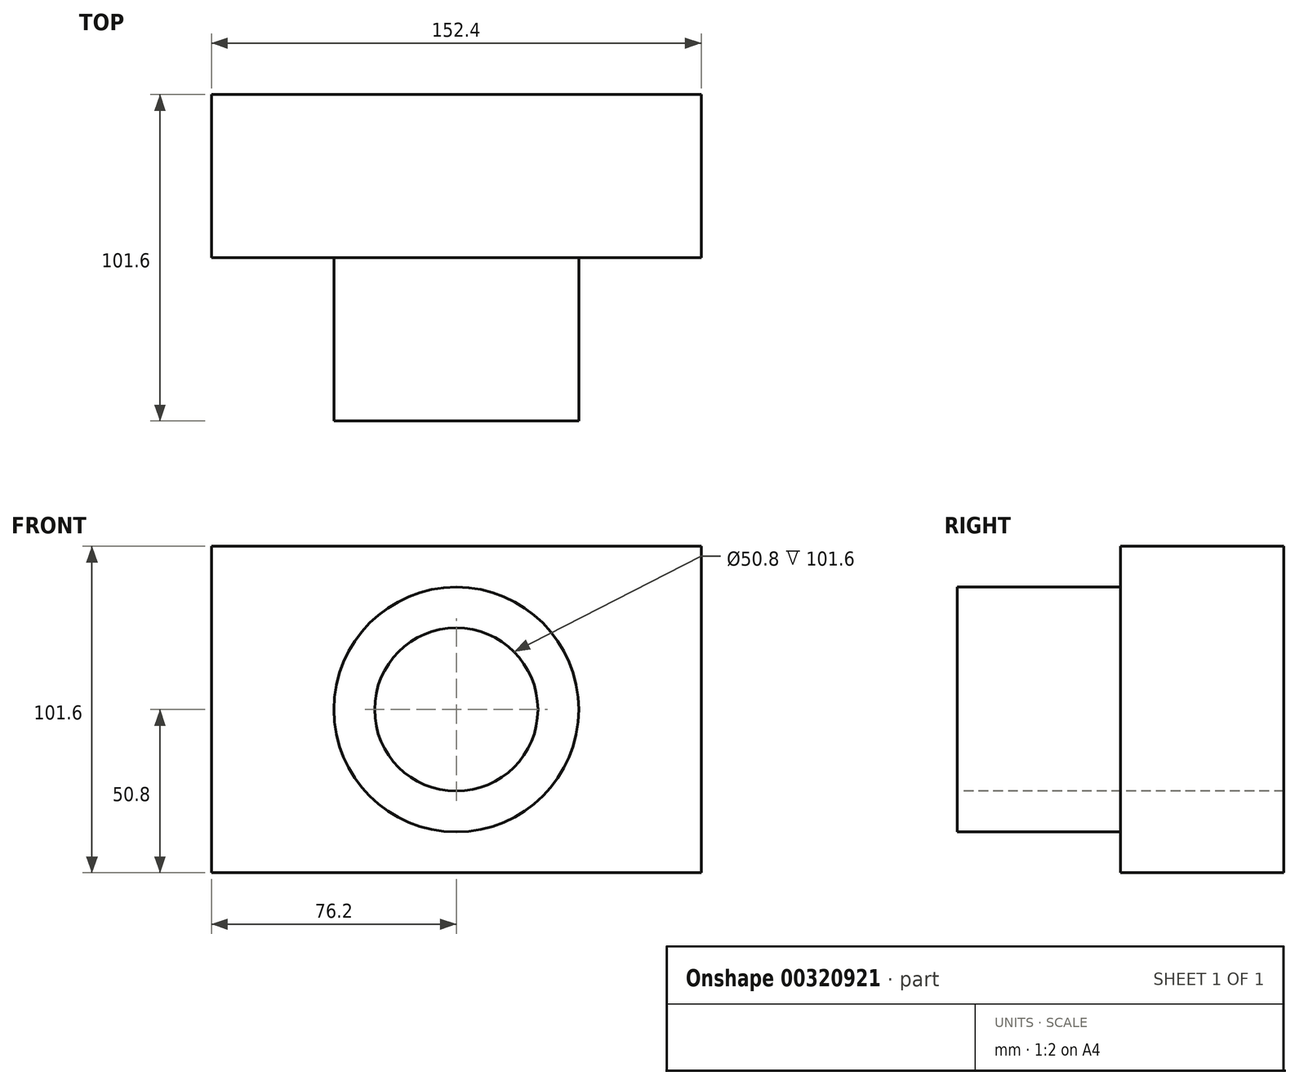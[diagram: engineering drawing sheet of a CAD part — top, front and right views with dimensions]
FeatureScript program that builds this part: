
annotation { "Feature Type Name" : "Feature", "Feature Type Description" : "" }
export const myFeature = defineFeature(function(context is Context, id is Id, definition is map)
    precondition{}
    {
        {
            var Q0;
            Q0=qCreatedBy(makeId("Front.planeOp"),FACE);
            var sketch = newSketch(context, id + "F0", { "sketchPlane" : qUnion([Q0])});
            skLineSegment(sketch, "E0.bottom", {"start": v(-76.2, 50.8) * mm, "end": v(76.2, 50.8) * mm});
            skLineSegment(sketch, "E0.top", {"start": v(-76.2, -50.8) * mm, "end": v(76.2, -50.8) * mm});
            skLineSegment(sketch, "E0.left", {"start": v(-76.2, 50.8) * mm, "end": v(-76.2, -50.8) * mm});
            skLineSegment(sketch, "E0.right", {"start": v(76.2, 50.8) * mm, "end": v(76.2, -50.8) * mm});
            skSolve(sketch);
        }
        {
            var Q0;
            Q0=makeQuery(id+"F0.imprint","IMPRINT",FACE,{"disambiguationData":[TD([[makeQuery(id+"F0.imprint","IMPRINT",EDGE,{"derivedFrom":sQuery(id+"F0.wireOp",EDGE,"E0.bottom")}),-1.0]])]});
            extrude(context, id + "F1", {"entities" : qUnion([Q0]), "depth" : 50.8 * mm});
        }
        {
            var Q0;
            Q0=makeQuery(id+"F1.opExtrude","CAP_FACE",FACE,{"disambiguationData":[OSD([sQuery(id+"F0.wireOp",EDGE,"E0.bottom"),sQuery(id+"F0.wireOp",EDGE,"E0.top"),sQuery(id+"F0.wireOp",EDGE,"E0.left"),sQuery(id+"F0.wireOp",EDGE,"E0.right")])],"isStart":false});
            var sketch = newSketch(context, id + "F2", { "sketchPlane" : qUnion([Q0])});
            skSolve(sketch);
        }
        {
            var Q0;
            Q0=makeQuery(id+"F2.imprint","IMPRINT",FACE,{"disambiguationData":[TD([[makeQuery(id+"F2.imprint","IMPRINT",EDGE,{"derivedFrom":makeQuery(id+"F1.opExtrude","CAP_EDGE",EDGE,{"disambiguationData":[OSD([sQuery(id+"F0.wireOp",EDGE,"E0.bottom")])],"isStart":false})}),-1.0]])]});
            var sketch = newSketch(context, id + "F3", { "sketchPlane" : qUnion([Q0])});
            skCircle(sketch, "E1", {"center": v(0, 0) * mm, "radius": 38.1 * mm});
            skSolve(sketch);
        }
        {
            var Q0;
            Q0=makeQuery(id+"F3.imprint","IMPRINT",FACE,{"disambiguationData":[TD([[makeQuery(id+"F3.imprint","IMPRINT",EDGE,{"derivedFrom":sQuery(id+"F3.wireOp",EDGE,"E1")}),1.0]])]});
            extrude(context, id + "F4", {"entities" : qUnion([Q0]), "operationType" : NewBodyOperationType.ADD, "depth" : 50.8 * mm});
        }
        {
            var Q0;
            Q0=makeQuery(id+"F4.opExtrude","CAP_FACE",FACE,{"disambiguationData":[OSD([sQuery(id+"F3.wireOp",EDGE,"E1")])],"isStart":false});
            var sketch = newSketch(context, id + "F5", { "sketchPlane" : qUnion([Q0])});
            skCircle(sketch, "E2", {"center": v(0, 0) * mm, "radius": 25.4 * mm});
            skSolve(sketch);
        }
        {
            var Q0;
            Q0=makeQuery(id+"F5.imprint","IMPRINT",FACE,{"disambiguationData":[TD([[makeQuery(id+"F5.imprint","IMPRINT",EDGE,{"derivedFrom":sQuery(id+"F5.wireOp",EDGE,"E2")}),1.0]])]});
            extrude(context, id + "F6", {"entities" : qUnion([Q0]), "operationType" : NewBodyOperationType.REMOVE, "oppositeDirection" : true, "depth" : 101.6 * mm});
        }
    });
